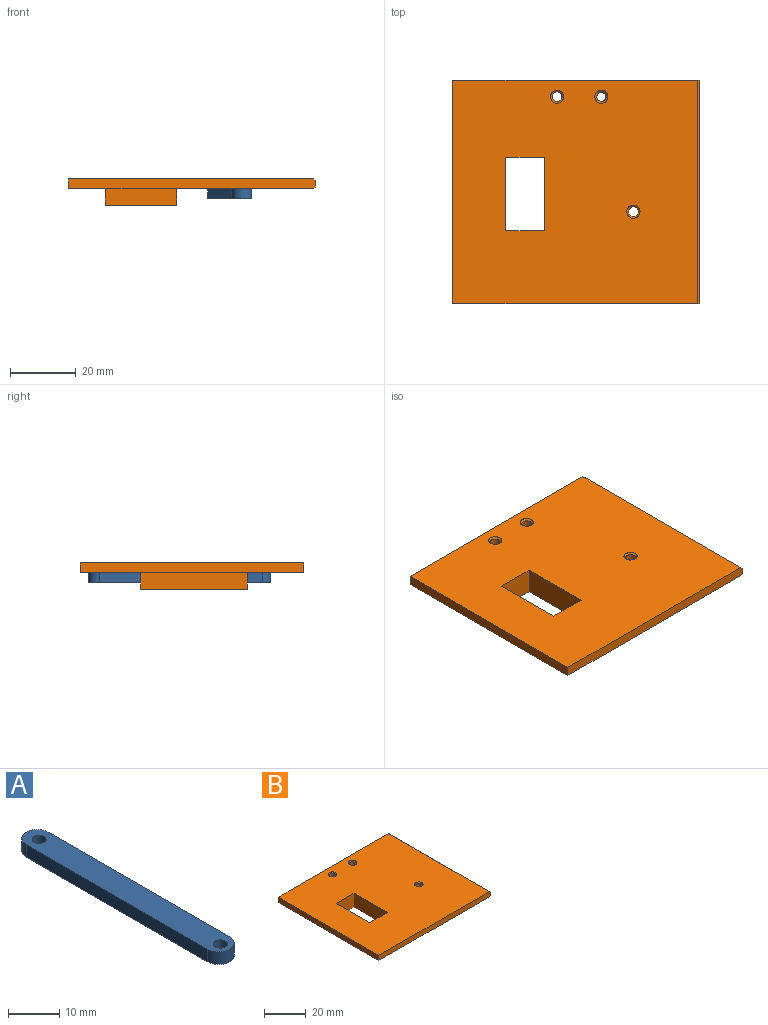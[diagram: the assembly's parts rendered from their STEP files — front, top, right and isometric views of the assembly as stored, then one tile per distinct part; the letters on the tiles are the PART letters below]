
ASSEMBLY  parts=2 mates=1
PART A: 8 faces, bbox 6x56x3 mm
  f0: cylinder r=3mm len=6mm, axis (0,0,-1), area 28.3mm2, adj f2,f3,f4,f5
  f1: cylinder r=3mm len=6mm, axis (0,0,-1), area 28.3mm2, adj f2,f3,f4,f5
  f2: plane 56x6mm, normal (0,0,1), area 316.4mm2, adj f0,f1,f4,f5,f6,f7
  f3: plane 56x6mm, normal (0,0,-1), area 316.4mm2, adj f0,f1,f4,f5,f6,f7
  f4: plane 50x3mm, normal (-1,0,0), area 150mm2, adj f0,f1,f2,f3
  f5: plane 50x3mm, normal (1,0,0), area 150mm2, adj f0,f1,f2,f3
  f6: cylinder r=1.38mm len=3mm, axis (0,0,-1), area 25.9mm2, adj f2,f3
  f7: cylinder r=1.38mm len=3mm, axis (0,0,-1), area 25.9mm2, adj f2,f3
PART B: 23 faces, bbox 75x68x8 mm
  f0: plane 74.51x68mm, normal (0,0,-1), area 4340.8mm2, adj f1,f2,f3,f7,f8,f9,f13,f14
  f1: plane 75.01x3mm, normal (0,1,0), area 224.8mm2, adj f0,f2,f11,f12,f21,f22
  f2: plane 68x3mm, normal (-1,0,0), area 204mm2, adj f0,f1,f3,f12
  f3: plane 75.01x3mm, normal (0,-1,0), area 224.8mm2, adj f0,f2,f11,f12,f21,f22
  f4: plane 11.75x8mm, normal (0,-1,0), area 94mm2, adj f5,f10,f12,f17
  f5: plane 22.4x8mm, normal (-1,0,0), area 179.2mm2, adj f4,f6,f12,f17
  f6: plane 11.75x8mm, normal (0,1,0), area 94mm2, adj f5,f10,f12,f17
  f7: cylinder r=1.5mm len=3mm, axis (0,0,-1), area 23.6mm2, adj f0,f20
  f8: cylinder r=1.5mm len=3mm, axis (0,0,-1), area 23.6mm2, adj f0,f19
  f9: cylinder r=1.5mm len=3mm, axis (0,0,-1), area 23.6mm2, adj f0,f18
  f10: plane 22.4x8mm, normal (1,0,0), area 179.2mm2, adj f4,f6,f12,f17
  f11: plane 68x2mm, normal (1,0,0), area 136mm2, adj f1,f3,f21,f22
  f12: plane 74.51x68mm, normal (0,0,1), area 4765.8mm2, adj f1,f2,f3,f4,f5,f6,f10,f18
  f13: plane 32.4x5mm, normal (-1,0,0), area 162mm2, adj f0,f14,f16,f17
  f14: plane 21.75x5mm, normal (0,1,0), area 108.8mm2, adj f0,f13,f15,f17
  f15: plane 32.4x5mm, normal (1,0,0), area 162mm2, adj f0,f14,f16,f17
  f16: plane 21.75x5mm, normal (0,-1,0), area 108.8mm2, adj f0,f13,f15,f17
  f17: plane 32.4x21.75mm, normal (0,0,-1), area 441.5mm2, adj f4,f5,f6,f10,f13,f14,f15,f16
  f18: cone r=1.5mm half-angle=45deg, axis (0,0,1), area 7.8mm2, adj f9,f12
  f19: cone r=1.5mm half-angle=45deg, axis (0,0,1), area 7.8mm2, adj f8,f12
  f20: cone r=1.5mm half-angle=45deg, axis (0,0,1), area 7.8mm2, adj f7,f12
  f21: plane 68x0.5mm, normal (0.71,0,-0.71), area 48.1mm2, adj f0,f1,f3,f11
  f22: plane 68x0.5mm, normal (0.71,0,0.71), area 48.1mm2, adj f1,f3,f11,f12
PLACE A rot(axis=(0,0,-1),171.6deg) t=(-1.94,-15.26,-2.93)mm
PLACE B t=(-7.73,-5.08,0.07)mm fixed
MATE cylindrical A.f7 <-> B.f8  axis (0,0,1) through (0,23.92,0.07)mm
